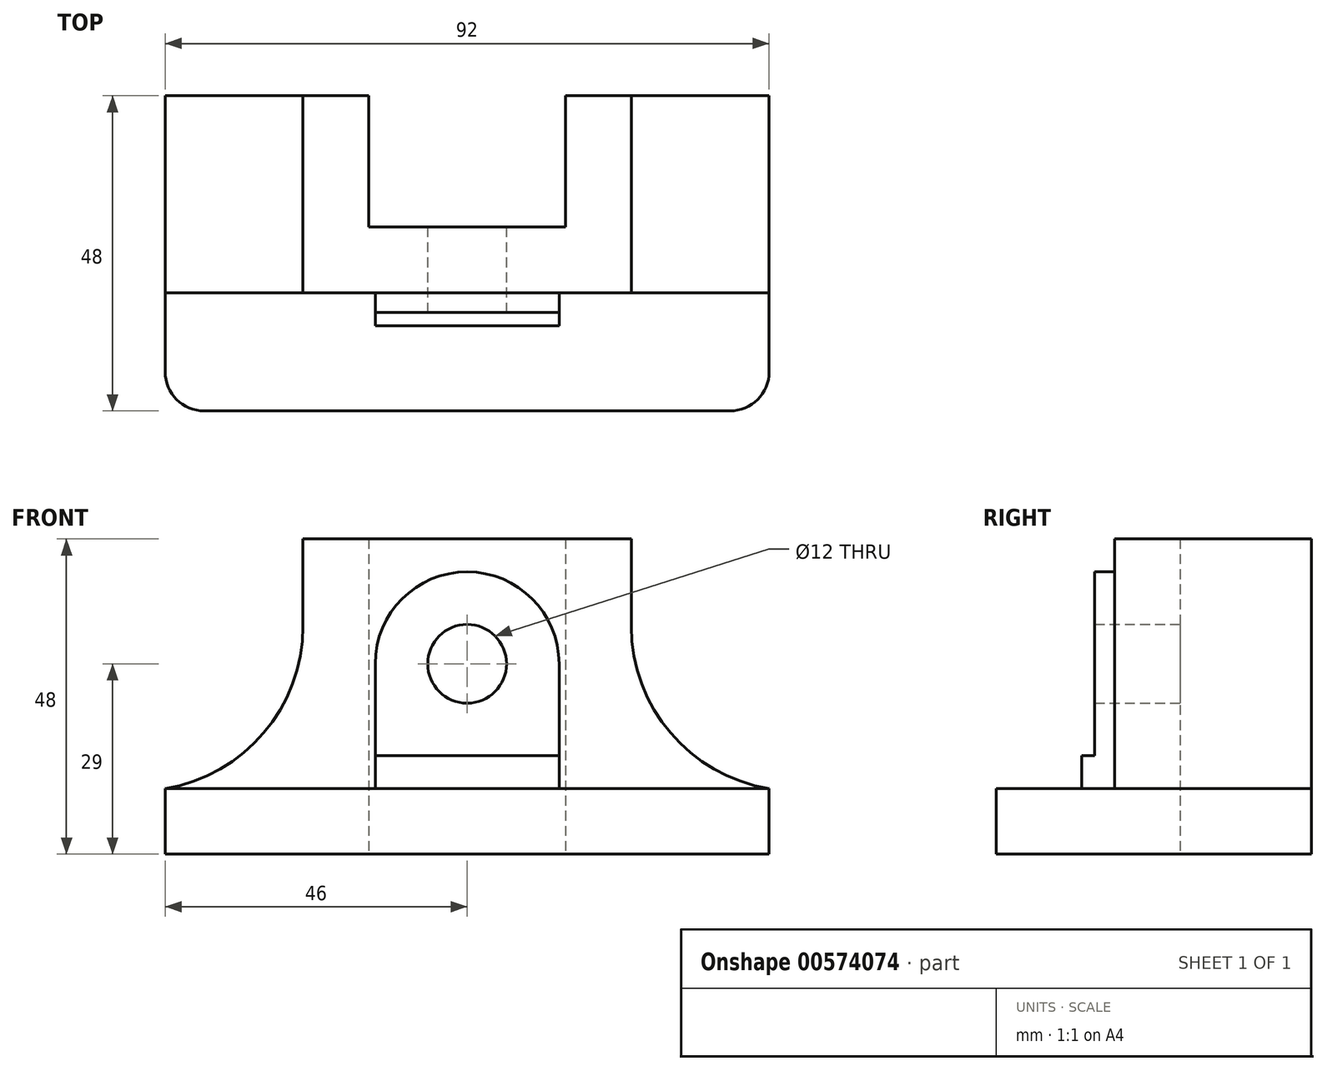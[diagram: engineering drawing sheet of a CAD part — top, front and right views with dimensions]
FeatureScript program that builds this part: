
annotation { "Feature Type Name" : "Feature", "Feature Type Description" : "" }
export const myFeature = defineFeature(function(context is Context, id is Id, definition is map)
    precondition{}
    {
        {
            var Q0;
            Q0=qCreatedBy(makeId("Top.planeOp"),FACE);
            var sketch = newSketch(context, id + "F0", { "sketchPlane" : qUnion([Q0])});
            skLineSegment(sketch, "E0.bottom", {"start": v(-46, 30) * mm, "end": v(-15, 30) * mm});
            skLineSegment(sketch, "E0.top", {"start": v(-40, -18) * mm, "end": v(40, -18) * mm});
            skLineSegment(sketch, "E0.left", {"start": v(-46, 30) * mm, "end": v(-46, -12) * mm});
            skLineSegment(sketch, "E0.right", {"start": v(46, 30) * mm, "end": v(46, -12) * mm});
            skPoint(sketch, "E1.visualSharp", {"position": v(-46, -18) * mm});
            skArc(sketch, "E1.filletArc", {"start": v(-46, -12) * mm, "mid": v(-44.24, -16.24) * mm, "end": v(-40, -18) * mm});
            skPoint(sketch, "E2.visualSharp", {"position": v(46, -18) * mm});
            skArc(sketch, "E2.filletArc", {"start": v(40, -18) * mm, "mid": v(44.24, -16.24) * mm, "end": v(46, -12) * mm});
            skLineSegment(sketch, "E3", {"start": v(-15, 30) * mm, "end": v(-15, 10) * mm});
            skLineSegment(sketch, "E4", {"start": v(15, 10) * mm, "end": v(15, 30) * mm});
            skLineSegment(sketch, "E5.trimOffspring", {"start": v(15, 30) * mm, "end": v(46, 30) * mm});
            skLineSegment(sketch, "E6", {"start": v(-15, 10) * mm, "end": v(15, 10) * mm});
            skSolve(sketch);
        }
        {
            var Q0;
            Q0 = qSketchRegion(id + "F0", true);
            extrude(context, id + "F1", {"entities" : qUnion([Q0]), "depth" : 10 * mm, "offsetDistance" : 25 * mm});
        }
        {
            var Q0;
            Q0=qCreatedBy(makeId("Top.planeOp"),FACE);
            var sketch = newSketch(context, id + "F2", { "sketchPlane" : qUnion([Q0])});
            skLineSegment(sketch, "E7", {"start": v(-25, 30) * mm, "end": v(-25, 0) * mm});
            skLineSegment(sketch, "E8", {"start": v(-25, 0) * mm, "end": v(25, 0) * mm});
            skLineSegment(sketch, "E9", {"start": v(25, 0) * mm, "end": v(25, 30) * mm});
            skLineSegment(sketch, "E10", {"start": v(25, 30) * mm, "end": v(15, 30) * mm});
            skLineSegment(sketch, "E11", {"start": v(15, 30) * mm, "end": v(15, 10) * mm});
            skLineSegment(sketch, "E12", {"start": v(-25, 30) * mm, "end": v(-15, 30) * mm});
            skLineSegment(sketch, "E13", {"start": v(-15, 30) * mm, "end": v(-15, 10) * mm});
            skLineSegment(sketch, "E14", {"start": v(-15, 10) * mm, "end": v(15, 10) * mm});
            skSolve(sketch);
        }
        {
            var Q0;
            Q0 = qSketchRegion(id + "F2", true);
            extrude(context, id + "F3", {"entities" : qUnion([Q0]), "operationType" : NewBodyOperationType.ADD, "depth" : 48 * mm, "offsetDistance" : 25 * mm});
        }
        {
            var Q0;
            Q0=makeQuery(id+"F3.boolean.opBoolean","INTERSECT",EDGE,{"derivedFrom":[makeQuery(id+"F1.opExtrude","CAP_FACE",FACE,{"disambiguationData":[OSD([sQuery(id+"F0.wireOp",EDGE,"E0.bottom"),sQuery(id+"F0.wireOp",EDGE,"E0.top"),sQuery(id+"F0.wireOp",EDGE,"E0.left"),sQuery(id+"F0.wireOp",EDGE,"E0.right"),sQuery(id+"F0.wireOp",EDGE,"E1.filletArc"),sQuery(id+"F0.wireOp",EDGE,"E2.filletArc"),sQuery(id+"F0.wireOp",EDGE,"E3"),sQuery(id+"F0.wireOp",EDGE,"E4"),sQuery(id+"F0.wireOp",EDGE,"E5.trimOffspring"),sQuery(id+"F0.wireOp",EDGE,"E6")])],"isStart":false}),makeQuery(id+"F3.opExtrude","SWEPT_FACE",FACE,{"disambiguationData":[OSD([sQuery(id+"F2.wireOp",EDGE,"E7")])]})]});
            fillet(context, id + "F4", {"entities" : qUnion([Q0]), "radius" : 25 * mm, "tangentPropagation" : true, "allowEdgeOverflow" : false});
        }
        {
            var Q0;
            Q0=makeQuery(id+"F3.boolean.opBoolean","INTERSECT",EDGE,{"derivedFrom":[makeQuery(id+"F1.opExtrude","CAP_FACE",FACE,{"disambiguationData":[OSD([sQuery(id+"F0.wireOp",EDGE,"E0.bottom"),sQuery(id+"F0.wireOp",EDGE,"E0.top"),sQuery(id+"F0.wireOp",EDGE,"E0.left"),sQuery(id+"F0.wireOp",EDGE,"E0.right"),sQuery(id+"F0.wireOp",EDGE,"E1.filletArc"),sQuery(id+"F0.wireOp",EDGE,"E2.filletArc"),sQuery(id+"F0.wireOp",EDGE,"E3"),sQuery(id+"F0.wireOp",EDGE,"E4"),sQuery(id+"F0.wireOp",EDGE,"E5.trimOffspring"),sQuery(id+"F0.wireOp",EDGE,"E6")])],"isStart":false}),makeQuery(id+"F3.opExtrude","SWEPT_FACE",FACE,{"disambiguationData":[OSD([sQuery(id+"F2.wireOp",EDGE,"E9")])]})]});
            fillet(context, id + "F5", {"entities" : qUnion([Q0]), "radius" : 25 * mm, "tangentPropagation" : true, "allowEdgeOverflow" : false});
        }
        {
            var Q0;
            Q0=makeQuery(id+"F3.opExtrude","SWEPT_FACE",FACE,{"disambiguationData":[OSD([sQuery(id+"F2.wireOp",EDGE,"E8")])]});
            var sketch = newSketch(context, id + "F6", { "sketchPlane" : qUnion([Q0])});
            skCircle(sketch, "E15", {"center": v(0, 29) * mm, "radius": 6 * mm});
            skArc(sketch, "E16", {"start": v(14, 29) * mm, "mid": v(0, 43) * mm, "end": v(-14, 29) * mm});
            skLineSegment(sketch, "E17", {"start": v(-14, 29) * mm, "end": v(-14, 10) * mm});
            skLineSegment(sketch, "E18", {"start": v(-14, 10) * mm, "end": v(14, 10) * mm});
            skLineSegment(sketch, "E19", {"start": v(14, 10) * mm, "end": v(14, 29) * mm});
            skSolve(sketch);
        }
        {
            var Q0;
            Q0 = qSketchRegion(id + "F6", true);
            extrude(context, id + "F7", {"entities" : qUnion([Q0]), "operationType" : NewBodyOperationType.ADD, "depth" : 3 * mm, "offsetDistance" : 25 * mm});
        }
        {
            var Q0;
            Q0=makeQuery(id+"F7.opExtrude","CAP_FACE",FACE,{"disambiguationData":[OSD([sQuery(id+"F6.wireOp",EDGE,"E15"),sQuery(id+"F6.wireOp",EDGE,"E16"),sQuery(id+"F6.wireOp",EDGE,"E17"),sQuery(id+"F6.wireOp",EDGE,"E18"),sQuery(id+"F6.wireOp",EDGE,"E19")])],"isStart":false});
            var sketch = newSketch(context, id + "F8", { "sketchPlane" : qUnion([Q0])});
            skLineSegment(sketch, "E20", {"start": v(-14, 15) * mm, "end": v(14, 15) * mm});
            skLineSegment(sketch, "E21", {"start": v(-14, 15) * mm, "end": v(-14, 10) * mm});
            skLineSegment(sketch, "E22", {"start": v(-14, 10) * mm, "end": v(14, 10) * mm});
            skLineSegment(sketch, "E23", {"start": v(14, 10) * mm, "end": v(14, 15) * mm});
            skSolve(sketch);
        }
        {
            var Q0;
            Q0 = qSketchRegion(id + "F8", true);
            extrude(context, id + "F9", {"entities" : qUnion([Q0]), "operationType" : NewBodyOperationType.ADD, "depth" : 2 * mm, "offsetDistance" : 25 * mm});
        }
        {
            var Q0;
            Q0=makeQuery(id+"F7.boolean.opBoolean","SPLIT",FACE,{"disambiguationData":[TD([makeQuery(id+"F7.opExtrude","SWEPT_FACE",FACE,{"disambiguationData":[OSD([sQuery(id+"F6.wireOp",EDGE,"E15")])]})])],"derivedFrom":makeQuery(id+"F3.opExtrude","SWEPT_FACE",FACE,{"disambiguationData":[OSD([sQuery(id+"F2.wireOp",EDGE,"E8")])]})});
            extrude(context, id + "F10", {"entities" : qUnion([Q0]), "operationType" : NewBodyOperationType.REMOVE, "oppositeDirection" : true, "depth" : 25 * mm, "offsetDistance" : 25 * mm});
        }
    });
